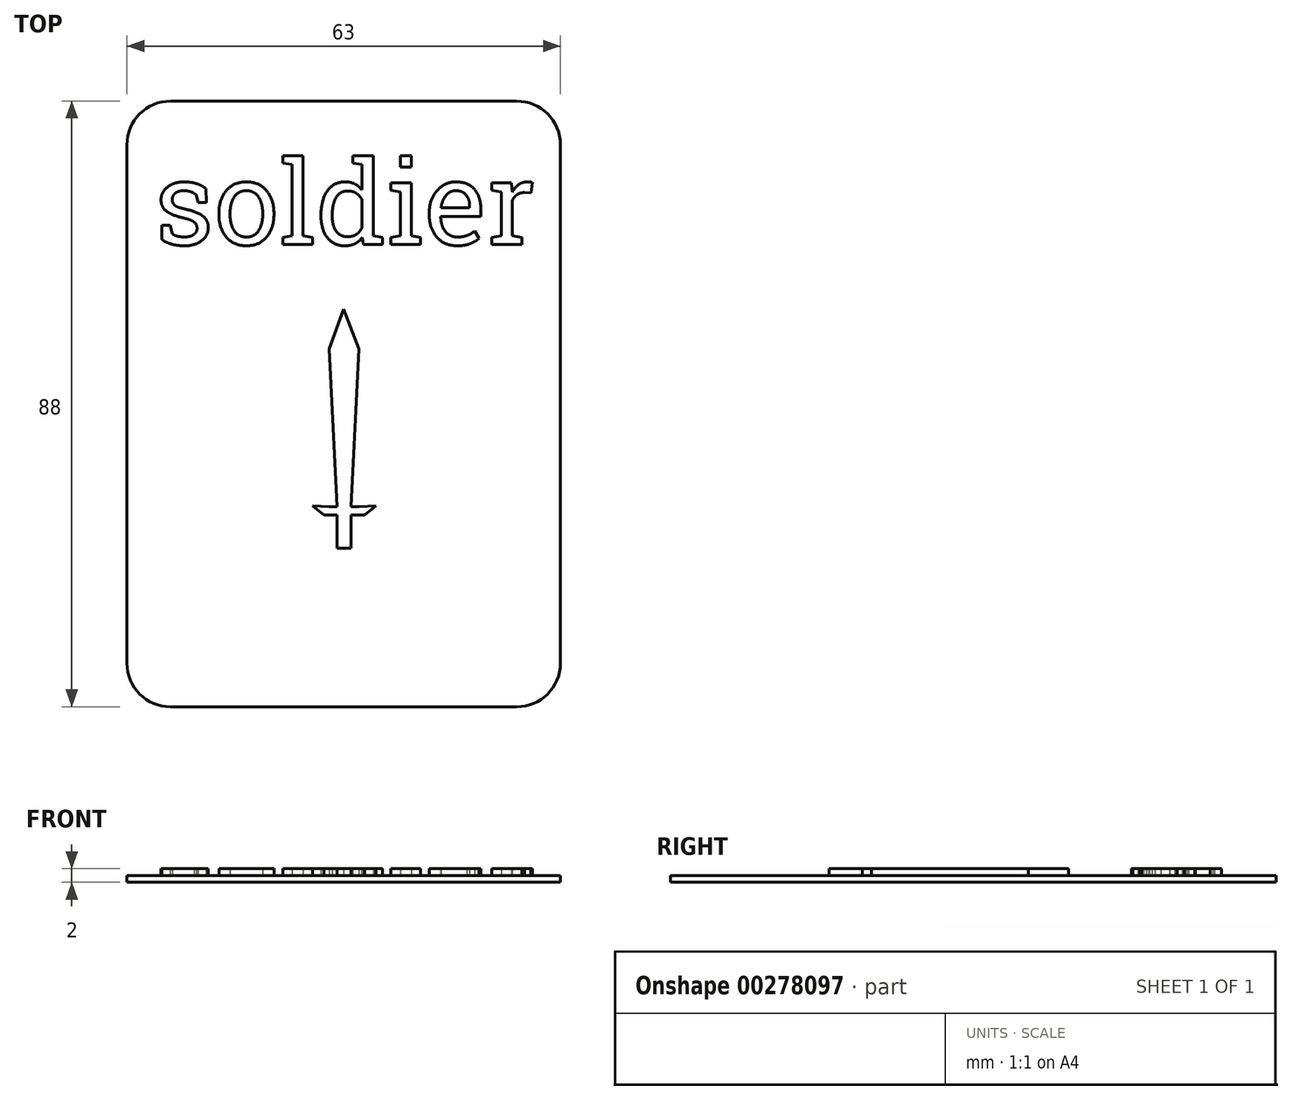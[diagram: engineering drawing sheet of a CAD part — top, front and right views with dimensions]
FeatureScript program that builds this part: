
annotation { "Feature Type Name" : "Feature", "Feature Type Description" : "" }
export const myFeature = defineFeature(function(context is Context, id is Id, definition is map)
    precondition{}
    {
        {
            var Q0;
            Q0=qCreatedBy(makeId("Top.planeOp"),FACE);
            var sketch = newSketch(context, id + "F0", { "sketchPlane" : qUnion([Q0])});
            skLineSegment(sketch, "E0.bottom", {"start": v(-41.55, 61.25) * mm, "end": v(8.75, 61.25) * mm});
            skLineSegment(sketch, "E0.top", {"start": v(-41.55, -26.75) * mm, "end": v(8.75, -26.75) * mm});
            skLineSegment(sketch, "E0.left", {"start": v(-47.9, 54.9) * mm, "end": v(-47.9, -20.4) * mm});
            skLineSegment(sketch, "E0.right", {"start": v(15.1, 54.9) * mm, "end": v(15.1, -20.4) * mm});
            skPoint(sketch, "E1.visualSharp", {"position": v(-47.9, 61.25) * mm});
            skArc(sketch, "E1.filletArc", {"start": v(-41.55, 61.25) * mm, "mid": v(-46.05, 59.39) * mm, "end": v(-47.9, 54.9) * mm});
            skPoint(sketch, "E2.visualSharp", {"position": v(15.1, 61.25) * mm});
            skArc(sketch, "E2.filletArc", {"start": v(15.1, 54.9) * mm, "mid": v(13.24, 59.39) * mm, "end": v(8.75, 61.25) * mm});
            skPoint(sketch, "E3.visualSharp", {"position": v(15.1, -26.75) * mm});
            skArc(sketch, "E3.filletArc", {"start": v(8.75, -26.75) * mm, "mid": v(13.24, -24.9) * mm, "end": v(15.1, -20.4) * mm});
            skPoint(sketch, "E4.visualSharp", {"position": v(-47.9, -26.75) * mm});
            skArc(sketch, "E4.filletArc", {"start": v(-47.9, -20.4) * mm, "mid": v(-46.05, -24.9) * mm, "end": v(-41.55, -26.75) * mm});
            skSolve(sketch);
        }
        {
            var Q0;
            Q0 = qSketchRegion(id + "F0", true);
            extrude(context, id + "F1", {"entities" : qUnion([Q0]), "depth" : 1 * mm});
        }
        {
            var Q0;
            Q0=makeQuery(id+"F1.opExtrude","CAP_FACE",FACE,{"disambiguationData":[OSD([sQuery(id+"F0.wireOp",EDGE,"E0.bottom"),sQuery(id+"F0.wireOp",EDGE,"E0.top"),sQuery(id+"F0.wireOp",EDGE,"E0.left"),sQuery(id+"F0.wireOp",EDGE,"E0.right"),sQuery(id+"F0.wireOp",EDGE,"E1.filletArc"),sQuery(id+"F0.wireOp",EDGE,"E2.filletArc"),sQuery(id+"F0.wireOp",EDGE,"E3.filletArc"),sQuery(id+"F0.wireOp",EDGE,"E4.filletArc")])],"isStart":false});
            var sketch = newSketch(context, id + "F2", { "sketchPlane" : qUnion([Q0])});
            skLineSegment(sketch, "E5", {"start": v(-16.4, 31.05) * mm, "end": v(-16.4, 25.41) * mm});
            skLineSegment(sketch, "E6", {"start": v(-16.4, 31.05) * mm, "end": v(-18.54, 25.22) * mm});
            skLineSegment(sketch, "E7", {"start": v(-16.4, 31.05) * mm, "end": v(-14.2, 25.22) * mm});
            skLineSegment(sketch, "E8", {"start": v(-14.2, 2.34) * mm, "end": v(-18.54, 2.34) * mm});
            skLineSegment(sketch, "E9", {"start": v(-16.4, 25.41) * mm, "end": v(-16.4, -1.6) * mm});
            skLineSegment(sketch, "E10", {"start": v(-17.35, 2.34) * mm, "end": v(-17.35, -3.7) * mm});
            skLineSegment(sketch, "E11", {"start": v(-17.35, -3.7) * mm, "end": v(-16.4, -3.7) * mm});
            skLineSegment(sketch, "E12", {"start": v(-16.4, -3.7) * mm, "end": v(-16.4, -1.6) * mm});
            skLineSegment(sketch, "E13", {"start": v(-15.31, 2.34) * mm, "end": v(-15.31, -3.7) * mm});
            skLineSegment(sketch, "E14", {"start": v(-15.31, -3.7) * mm, "end": v(-16.4, -3.7) * mm});
            skLineSegment(sketch, "E15", {"start": v(-14.2, 2.34) * mm, "end": v(-11.73, 2.45) * mm});
            skLineSegment(sketch, "E16", {"start": v(-11.73, 2.45) * mm, "end": v(-13.39, 1.1) * mm});
            skLineSegment(sketch, "E17", {"start": v(-13.39, 1.1) * mm, "end": v(-15.31, 1.1) * mm});
            skLineSegment(sketch, "E18", {"start": v(-18.54, 2.34) * mm, "end": v(-20.95, 2.45) * mm});
            skLineSegment(sketch, "E19", {"start": v(-20.95, 2.45) * mm, "end": v(-19.3, 1.1) * mm});
            skLineSegment(sketch, "E20", {"start": v(-19.3, 1.1) * mm, "end": v(-17.35, 1.1) * mm});
            skLineSegment(sketch, "E21", {"start": v(-14.2, 25.22) * mm, "end": v(-15.31, 2.34) * mm});
            skLineSegment(sketch, "E22", {"start": v(-18.54, 25.22) * mm, "end": v(-17.35, 2.34) * mm});
            skSolve(sketch);
        }
        {
            var Q0;
            Q0 = qSketchRegion(id + "F2", true);
            extrude(context, id + "F3", {"entities" : qUnion([Q0]), "operationType" : NewBodyOperationType.ADD, "depth" : 1 * mm});
        }
        {
            var Q0;
            Q0=makeQuery(id+"F1.opExtrude","CAP_FACE",FACE,{"disambiguationData":[OSD([sQuery(id+"F0.wireOp",EDGE,"E0.bottom"),sQuery(id+"F0.wireOp",EDGE,"E0.top"),sQuery(id+"F0.wireOp",EDGE,"E0.left"),sQuery(id+"F0.wireOp",EDGE,"E0.right"),sQuery(id+"F0.wireOp",EDGE,"E1.filletArc"),sQuery(id+"F0.wireOp",EDGE,"E2.filletArc"),sQuery(id+"F0.wireOp",EDGE,"E3.filletArc"),sQuery(id+"F0.wireOp",EDGE,"E4.filletArc")])],"isStart":false});
            var sketch = newSketch(context, id + "F4", { "sketchPlane" : qUnion([Q0])});
            skText(sketch, "E23", { "text": "soldier", "fontName": "RobotoSlab-Regular.ttf"});
            const initialGuessF4  = {"E23": [-0.04393, 0.0404, 1, 0, 0.0122]};
            skSetInitialGuess(sketch, initialGuessF4);
            skSolve(sketch);
        }
        {
            var Q0;
            Q0 = qSketchRegion(id + "F4", true);
            extrude(context, id + "F5", {"entities" : qUnion([Q0]), "operationType" : NewBodyOperationType.ADD, "depth" : 1 * mm});
        }
    });
